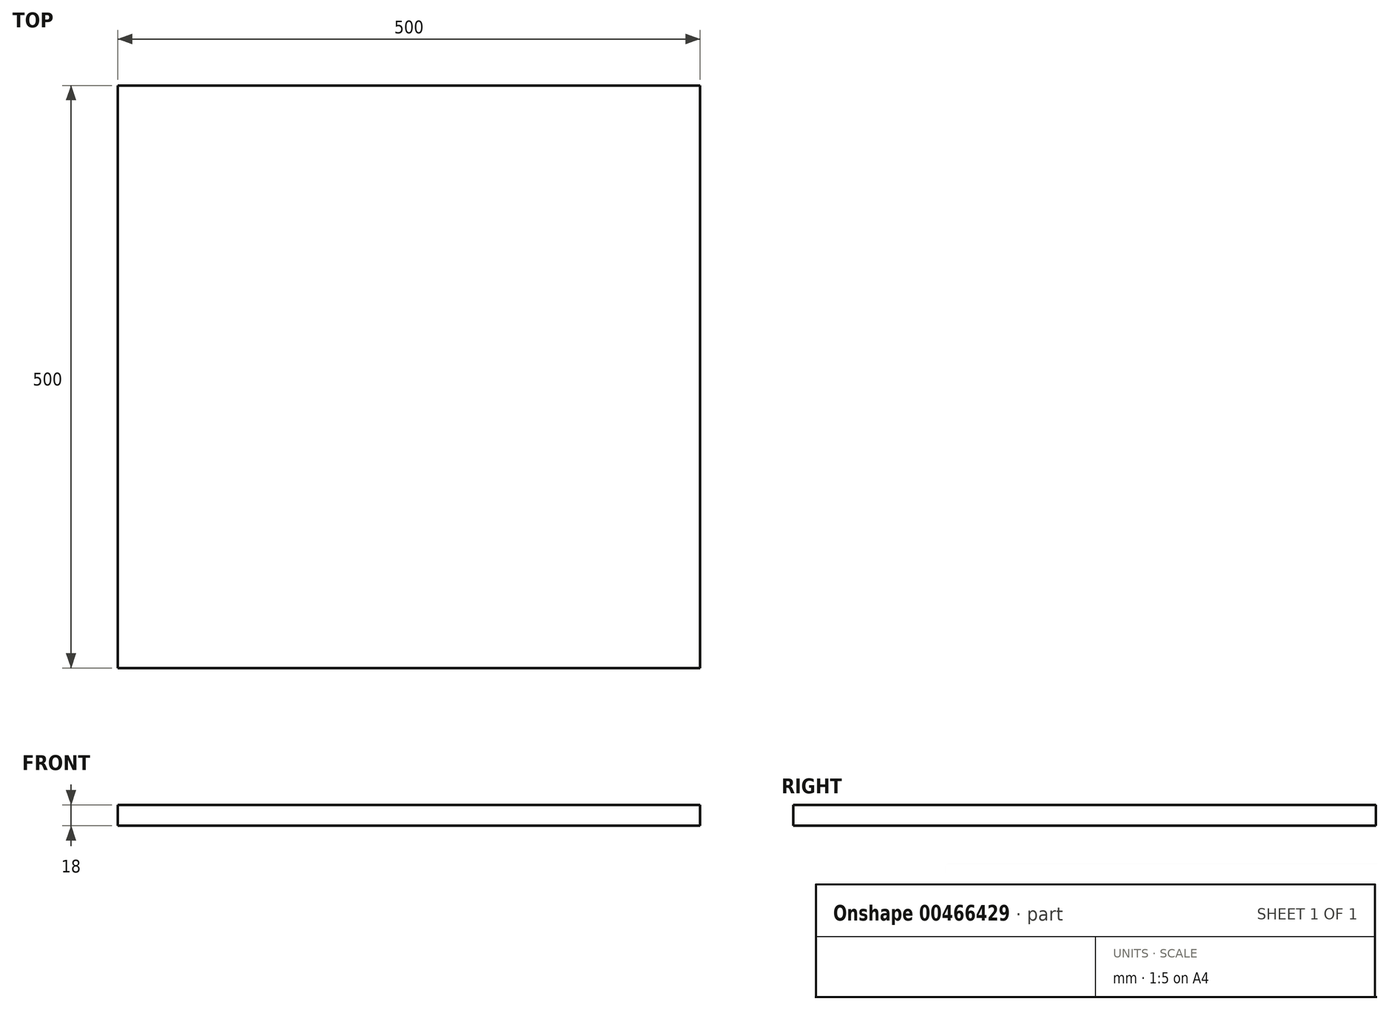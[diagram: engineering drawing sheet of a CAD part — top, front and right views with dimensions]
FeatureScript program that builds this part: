
annotation { "Feature Type Name" : "Feature", "Feature Type Description" : "" }
export const myFeature = defineFeature(function(context is Context, id is Id, definition is map)
    precondition{}
    {
        {
            var Q0;
            Q0=qCreatedBy(makeId("Top.planeOp"),FACE);
            var sketch = newSketch(context, id + "F0", { "sketchPlane" : qUnion([Q0])});
            skLineSegment(sketch, "E0.bottom", {"start": v(0, 0) * mm, "end": v(500, 0) * mm});
            skLineSegment(sketch, "E0.top", {"start": v(0, -500) * mm, "end": v(500, -500) * mm});
            skLineSegment(sketch, "E0.left", {"start": v(0, 0) * mm, "end": v(0, -500) * mm});
            skLineSegment(sketch, "E0.right", {"start": v(500, 0) * mm, "end": v(500, -500) * mm});
            skSolve(sketch);
        }
        {
            var Q0;
            Q0=makeQuery(id+"F0.imprint","IMPRINT",FACE,{"disambiguationData":[TD([[makeQuery(id+"F0.imprint","IMPRINT",EDGE,{"derivedFrom":sQuery(id+"F0.wireOp",EDGE,"E0.bottom")}),-1.0]])]});
            extrude(context, id + "F1", {"entities" : qUnion([Q0]), "depth" : 18 * mm});
        }
    });
